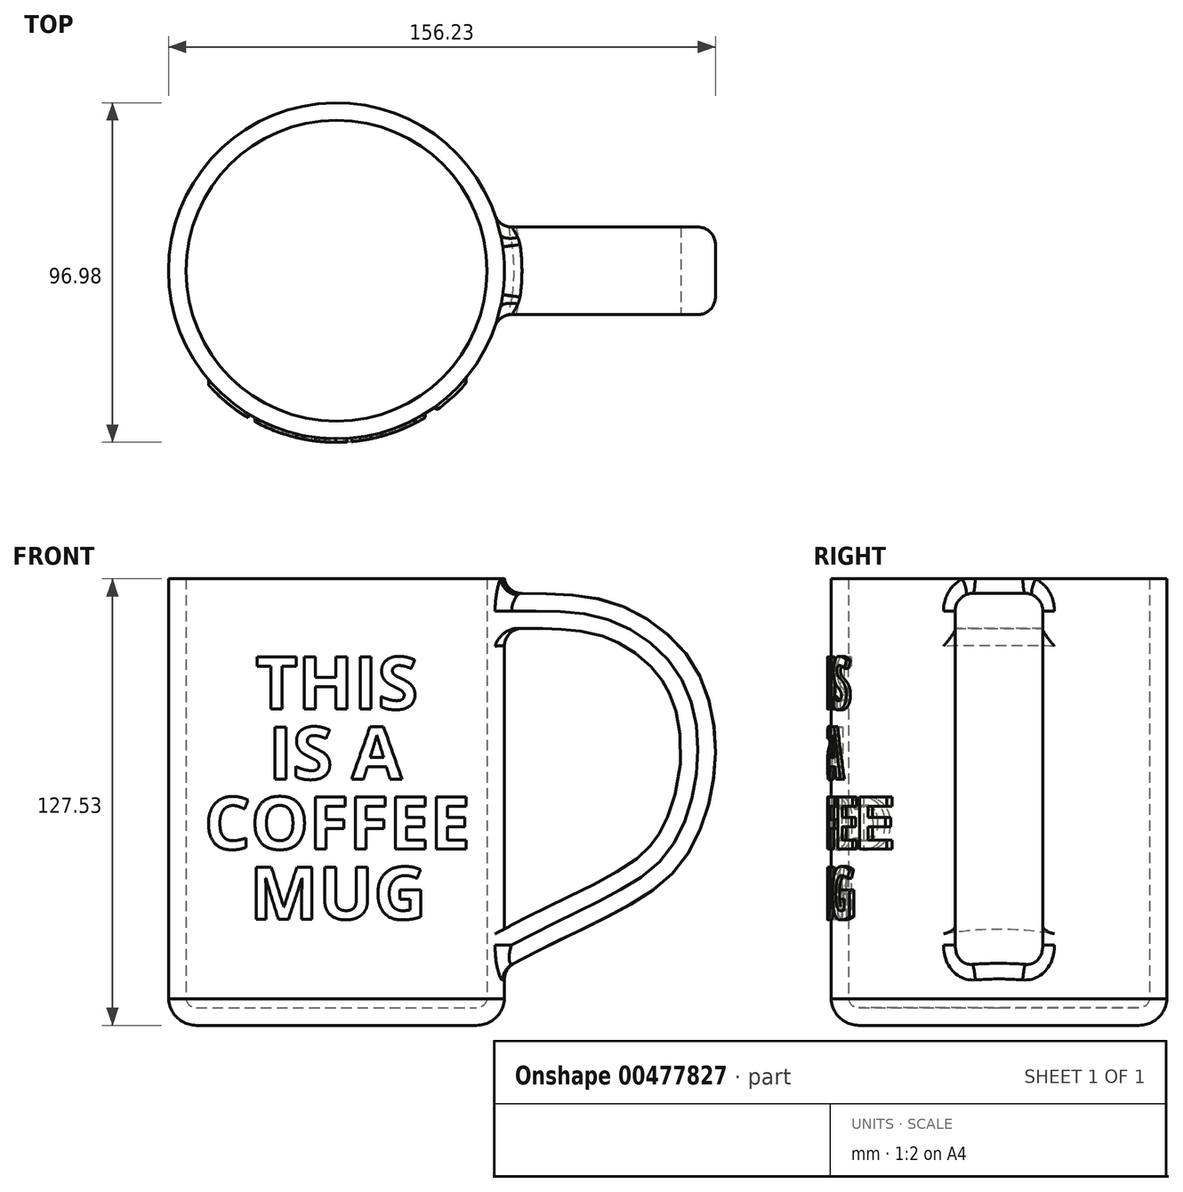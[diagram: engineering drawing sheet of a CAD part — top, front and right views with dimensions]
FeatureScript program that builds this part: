
annotation { "Feature Type Name" : "Feature", "Feature Type Description" : "" }
export const myFeature = defineFeature(function(context is Context, id is Id, definition is map)
    precondition{}
    {
        {
            var Q0;
            Q0=qCreatedBy(makeId("Front.planeOp"),FACE);
            var sketch = newSketch(context, id + "F0", { "sketchPlane" : qUnion([Q0])});
            skLineSegment(sketch, "E0", {"start": v(0, 0) * mm, "end": v(-40, 0) * mm});
            skArc(sketch, "E1", {"start": v(-47.99, 7.53) * mm, "mid": v(-45.49, 2.18) * mm, "end": v(-40, 0) * mm});
            skLineSegment(sketch, "E2", {"start": v(-47.99, 7.53) * mm, "end": v(-47.99, 127.53) * mm});
            skLineSegment(sketch, "E3", {"start": v(-47.99, 127.53) * mm, "end": v(0, 127.53) * mm});
            skLineSegment(sketch, "E4", {"start": v(0, 0) * mm, "end": v(0, 127.53) * mm});
            skPoint(sketch, "E5.MirrorCS.start.orphan", {"position": v(0, 0) * mm});
            skSolve(sketch);
        }
        {
            var Q0;
            Q0=qCreatedBy(makeId("Front.planeOp"),FACE);
            var sketch = newSketch(context, id + "F1", { "sketchPlane" : qUnion([Q0])});
            skLineSegment(sketch, "E6", {"start": v(0, 0) * mm, "end": v(0, 62.98) * mm, "construction": true});
            skSolve(sketch);
        }
        {
            var Q0;
            Q0 = qSketchRegion(id + "F0", true);
            var Q1;
            Q1=sQuery(id+"F1.wireOp",EDGE,"E6");
            revolve(context, id + "F2", {"entities" : qUnion([Q0]), "axis" : qUnion([Q1]), "revolveType" : RevolveType.FULL});
        }
        {
            var Q0;
            Q0=makeQuery(id+"F2.opRevolve","SWEPT_FACE",FACE,{"disambiguationData":[OSD([sQuery(id+"F0.wireOp",EDGE,"E3")])]});
            shell(context, id + "F3", {"entities" : qUnion([Q0]), "thickness" : 5 * mm});
        }
        {
            var Q0;
            Q0=qCreatedBy(makeId("Front.planeOp"),FACE);
            var sketch = newSketch(context, id + "F4", { "sketchPlane" : qUnion([Q0])});
            skFitSpline(sketch, "E7", {"points": [v(42.99, 123.16) * mm, v(64.31, 123.16) * mm, v(82.72, 119.24) * mm, v(102.03, 102.95) * mm, v(108.06, 73.98) * mm, v(99.31, 47.43) * mm, v(82.72, 33.85) * mm, v(59.79, 22.4) * mm, v(48.63, 16.66) * mm, v(42.99, 14.24) * mm], "startDerivative": vector(191.24, 5.01) * mm, "endDerivative": vector(-87.34, -34.84) * mm});
            skFitSpline(sketch, "E8.0", {"points": [v(43.25, 113.16) * mm, v(45.24, 113.22) * mm, v(49.19, 113.32) * mm, v(53.97, 113.39) * mm, v(57.66, 113.38) * mm, v(60.36, 113.32) * mm, v(62.54, 113.24) * mm, v(64.23, 113.15) * mm, v(65.87, 113.04) * mm, v(67.84, 112.86) * mm, v(70.81, 112.46) * mm, v(73.59, 111.88) * mm, v(76.3, 111.05) * mm, v(77.99, 110.4) * mm, v(79.37, 109.79) * mm, v(80.77, 109.1) * mm, v(82.54, 108.14) * mm, v(84.64, 106.8) * mm, v(86.68, 105.29) * mm, v(88.6, 103.64) * mm, v(90.38, 101.86) * mm, v(91.72, 100.28) * mm, v(92.68, 98.98) * mm, v(93.35, 97.98) * mm, v(93.97, 96.96) * mm, v(94.55, 95.88) * mm, v(95.09, 94.76) * mm, v(95.75, 93.2) * mm, v(96.48, 91.15) * mm, v(97.2, 88.53) * mm, v(97.72, 85.78) * mm, v(98.2, 81.96) * mm, v(98.33, 77) * mm, v(97.78, 70.97) * mm, v(96.78, 66.11) * mm, v(95.69, 62.46) * mm, v(94.74, 59.88) * mm, v(93.68, 57.48) * mm, v(92.72, 55.66) * mm, v(91.91, 54.34) * mm, v(91.3, 53.41) * mm, v(90.68, 52.55) * mm, v(89.81, 51.46) * mm, v(88.67, 50.19) * mm, v(87.14, 48.75) * mm, v(85.45, 47.37) * mm, v(82.9, 45.55) * mm, v(79.92, 43.73) * mm, v(76.47, 41.82) * mm, v(72.8, 39.9) * mm, v(68.92, 37.96) * mm, v(65, 36.05) * mm, v(62.1, 34.65) * mm, v(59.25, 33.28) * mm, v(56.98, 32.16) * mm, v(55.22, 31.29) * mm, v(53.53, 30.43) * mm, v(51.57, 29.42) * mm, v(49.44, 28.3) * mm, v(47.53, 27.3) * mm, v(46.13, 26.58) * mm, v(45.11, 26.07) * mm, v(44.53, 25.78) * mm, v(44.09, 25.57) * mm, v(43.65, 25.37) * mm, v(43.12, 25.13) * mm, v(42.5, 24.85) * mm, v(41.66, 24.5) * mm, v(40.61, 24.06) * mm, v(39.74, 23.71) * mm, v(39.28, 23.53) * mm]});
            skLineSegment(sketch, "E9", {"start": v(42.99, 123.16) * mm, "end": v(43.25, 113.16) * mm});
            skLineSegment(sketch, "E10", {"start": v(42.99, 25.07) * mm, "end": v(42.99, 14.24) * mm});
            skLineSegment(sketch, "E11.trimOffspring", {"start": v(42.99, 25.07) * mm, "end": v(42.99, 14.24) * mm, "construction": true});
            skSolve(sketch);
        }
        {
            var Q0;
            Q0 = qSketchRegion(id + "F4", true);
            extrude(context, id + "F5", {"entities" : qUnion([Q0]), "operationType" : NewBodyOperationType.ADD, "depth" : 25 * mm, "symmetric" : true});
        }
        {
            var Q0;
            Q0=makeQuery(id+"F5.opExtrude","CAP_EDGE",EDGE,{"disambiguationData":[OSD([sQuery(id+"F4.wireOp",EDGE,"E7")])],"isStart":true});
            var Q1;
            Q1=makeQuery(id+"F5.opExtrude","CAP_EDGE",EDGE,{"disambiguationData":[OSD([sQuery(id+"F4.wireOp",EDGE,"E7")])],"isStart":false});
            var Q2;
            Q2=makeQuery(id+"F5.boolean.opBoolean","INTERSECT",EDGE,{"disambiguationData":[OD(0.0)],"derivedFrom":[makeQuery(id+"F2.opRevolve","SWEPT_FACE",FACE,{"disambiguationData":[OSD([sQuery(id+"F0.wireOp",EDGE,"E2")])]}),makeQuery(id+"F5.opExtrude","SWEPT_FACE",FACE,{"disambiguationData":[OSD([sQuery(id+"F4.wireOp",EDGE,"E7")])]})]});
            var Q3;
            Q3=makeQuery(id+"F5.boolean.opBoolean","INTERSECT",EDGE,{"disambiguationData":[OD(0.0)],"derivedFrom":[makeQuery(id+"F2.opRevolve","SWEPT_FACE",FACE,{"disambiguationData":[OSD([sQuery(id+"F0.wireOp",EDGE,"E2")])]}),makeQuery(id+"F5.opExtrude","CAP_FACE",FACE,{"disambiguationData":[OSD([sQuery(id+"F4.wireOp",EDGE,"E7"),sQuery(id+"F4.wireOp",EDGE,"E8.0"),sQuery(id+"F4.wireOp",EDGE,"E9"),sQuery(id+"F4.wireOp",EDGE,"E10")])],"isStart":true})]});
            var Q4;
            Q4=makeQuery(id+"F5.boolean.opBoolean","INTERSECT",EDGE,{"disambiguationData":[OD(0.0)],"derivedFrom":[makeQuery(id+"F2.opRevolve","SWEPT_FACE",FACE,{"disambiguationData":[OSD([sQuery(id+"F0.wireOp",EDGE,"E2")])]}),makeQuery(id+"F5.opExtrude","CAP_FACE",FACE,{"disambiguationData":[OSD([sQuery(id+"F4.wireOp",EDGE,"E7"),sQuery(id+"F4.wireOp",EDGE,"E8.0"),sQuery(id+"F4.wireOp",EDGE,"E9"),sQuery(id+"F4.wireOp",EDGE,"E10")])],"isStart":false})]});
            fillet(context, id + "F6", {"entities" : qUnion([Q0, Q1, Q2, Q3, Q4]), "radius" : 5 * mm, "tangentPropagation" : true, "allowEdgeOverflow" : false});
        }
        {
            var Q0;
            Q0=makeQuery(id+"F5.boolean.opBoolean","INTERSECT",EDGE,{"disambiguationData":[OD(1.0)],"derivedFrom":[makeQuery(id+"F2.opRevolve","SWEPT_FACE",FACE,{"disambiguationData":[OSD([sQuery(id+"F0.wireOp",EDGE,"E2")])]}),makeQuery(id+"F5.opExtrude","SWEPT_FACE",FACE,{"disambiguationData":[OSD([sQuery(id+"F4.wireOp",EDGE,"E8.0")])]})]});
            var Q1;
            Q1=makeQuery(id+"F6.opFillet","BLEND_EDGE",EDGE,{"blendedFrom":[makeQuery(id+"F5.opExtrude","CAP_EDGE",EDGE,{"disambiguationData":[OSD([sQuery(id+"F4.wireOp",EDGE,"E7")])],"isStart":true}),makeQuery(id+"F2.opRevolve","SWEPT_FACE",FACE,{"disambiguationData":[OSD([sQuery(id+"F0.wireOp",EDGE,"E2")])]})],"blendedInto":[makeQuery(id+"F2.opRevolve","SWEPT_FACE",FACE,{"disambiguationData":[OSD([sQuery(id+"F0.wireOp",EDGE,"E2")])]})]});
            fillet(context, id + "F7", {"entities" : qUnion([Q0, Q1]), "radius" : 5 * mm, "tangentPropagation" : true, "allowEdgeOverflow" : false});
        }
        {
            var Q0;
            Q0=qCreatedBy(makeId("Front.planeOp"),FACE);
            cPlane(context, id + "F8", {"entities" : qUnion([Q0]), "cplaneType" : CPlaneType.OFFSET, "offset" : 30 * mm, "width" : 150 * mm, "height" : 150 * mm});
        }
        {
            var Q0;
            Q0=qCreatedBy(id+"F8.planeOp",FACE);
            var sketch = newSketch(context, id + "F9", { "sketchPlane" : qUnion([Q0])});
            skText(sketch, "E12", { "text": "THIS", "fontName": "OpenSans-Bold.ttf"});
            skText(sketch, "E13", { "text": "IS A", "fontName": "OpenSans-Bold.ttf"});
            skText(sketch, "E14", { "text": "COFFEE", "fontName": "OpenSans-Bold.ttf"});
            skText(sketch, "E15", { "text": "MUG", "fontName": "OpenSans-Bold.ttf"});
            skLineSegment(sketch, "E16", {"start": v(0.32, 70.32) * mm, "end": v(0.32, 65.32) * mm, "construction": true});
            skLineSegment(sketch, "E17", {"start": v(0.32, 50.32) * mm, "end": v(0.32, 45.32) * mm, "construction": true});
            skLineSegment(sketch, "E18", {"start": v(0.32, 90.32) * mm, "end": v(0.32, 85.32) * mm, "construction": true});
            skLineSegment(sketch, "E19", {"start": v(0, 0) * mm, "end": v(0.32, 75.23) * mm, "construction": true});
            const initialGuessF9  = {"E12": [-0.02313, 0.09032, 1, 0, 0.015], "E13": [-0.01944, 0.07032, 1, 0, 0.015], "E14": [-0.03777, 0.05032, 1, 0, 0.015], "E15": [-0.02476, 0.03032, 1, 0, 0.015]};
            skSetInitialGuess(sketch, initialGuessF9);
            skSolve(sketch);
        }
        {
            var Q0;
            Q0 = qSketchRegion(id + "F9", true);
            extrude(context, id + "F10", {"entities" : qUnion([Q0]), "operationType" : NewBodyOperationType.ADD, "depth" : 25 * mm});
        }
        {
            var Q0;
            Q0=qCreatedBy(makeId("Right.planeOp"),FACE);
            var sketch = newSketch(context, id + "F11", { "sketchPlane" : qUnion([Q0])});
            skLineSegment(sketch, "E20", {"start": v(0, 0) * mm, "end": v(-48.99, 0) * mm, "construction": true});
            skLineSegment(sketch, "E21", {"start": v(-48.99, 0) * mm, "end": v(-48.99, 119.85) * mm});
            skLineSegment(sketch, "E22", {"start": v(-48.99, 119.85) * mm, "end": v(-80.88, 119.85) * mm});
            skLineSegment(sketch, "E23", {"start": v(-80.88, 119.85) * mm, "end": v(-80.88, 0) * mm});
            skLineSegment(sketch, "E24", {"start": v(-80.88, 0) * mm, "end": v(-48.99, 0) * mm});
            skLineSegment(sketch, "E25", {"start": v(0, 0) * mm, "end": v(0, 115.98) * mm, "construction": true});
            skLineSegment(sketch, "E26", {"start": v(0, 0) * mm, "end": v(-34.86, 0) * mm, "construction": true});
            skLineSegment(sketch, "E27", {"start": v(0, 10.6) * mm, "end": v(-42.99, 10.6) * mm, "construction": true});
            skLineSegment(sketch, "E28", {"start": v(-42.99, 10.6) * mm, "end": v(-42.99, 119.55) * mm});
            skLineSegment(sketch, "E29", {"start": v(-42.99, 119.55) * mm, "end": v(-28.62, 119.55) * mm});
            skLineSegment(sketch, "E30", {"start": v(-28.62, 119.55) * mm, "end": v(-28.62, 10.6) * mm});
            skLineSegment(sketch, "E31", {"start": v(-28.62, 10.6) * mm, "end": v(-42.99, 10.6) * mm});
            skLineSegment(sketch, "E32", {"start": v(-47.99, 7.53) * mm, "end": v(-47.99, 127.53) * mm, "construction": true});
            skLineSegment(sketch, "E33", {"start": v(47.99, 127.53) * mm, "end": v(47.99, 7.53) * mm, "construction": true});
            skLineSegment(sketch, "E34", {"start": v(-47.99, 122.88) * mm, "end": v(47.99, 122.88) * mm, "construction": true});
            skSolve(sketch);
        }
        {
            var Q0;
            Q0 = qSketchRegion(id + "F11", true);
            var Q1;
            Q1=sQuery(id+"F11.wireOp",EDGE,"E25");
            revolve(context, id + "F12", {"operationType" : NewBodyOperationType.REMOVE, "entities" : qUnion([Q0]), "axis" : qUnion([Q1]), "revolveType" : RevolveType.SYMMETRIC, "oppositeDirection" : true, "angle" : 120 * degree});
        }
    });
